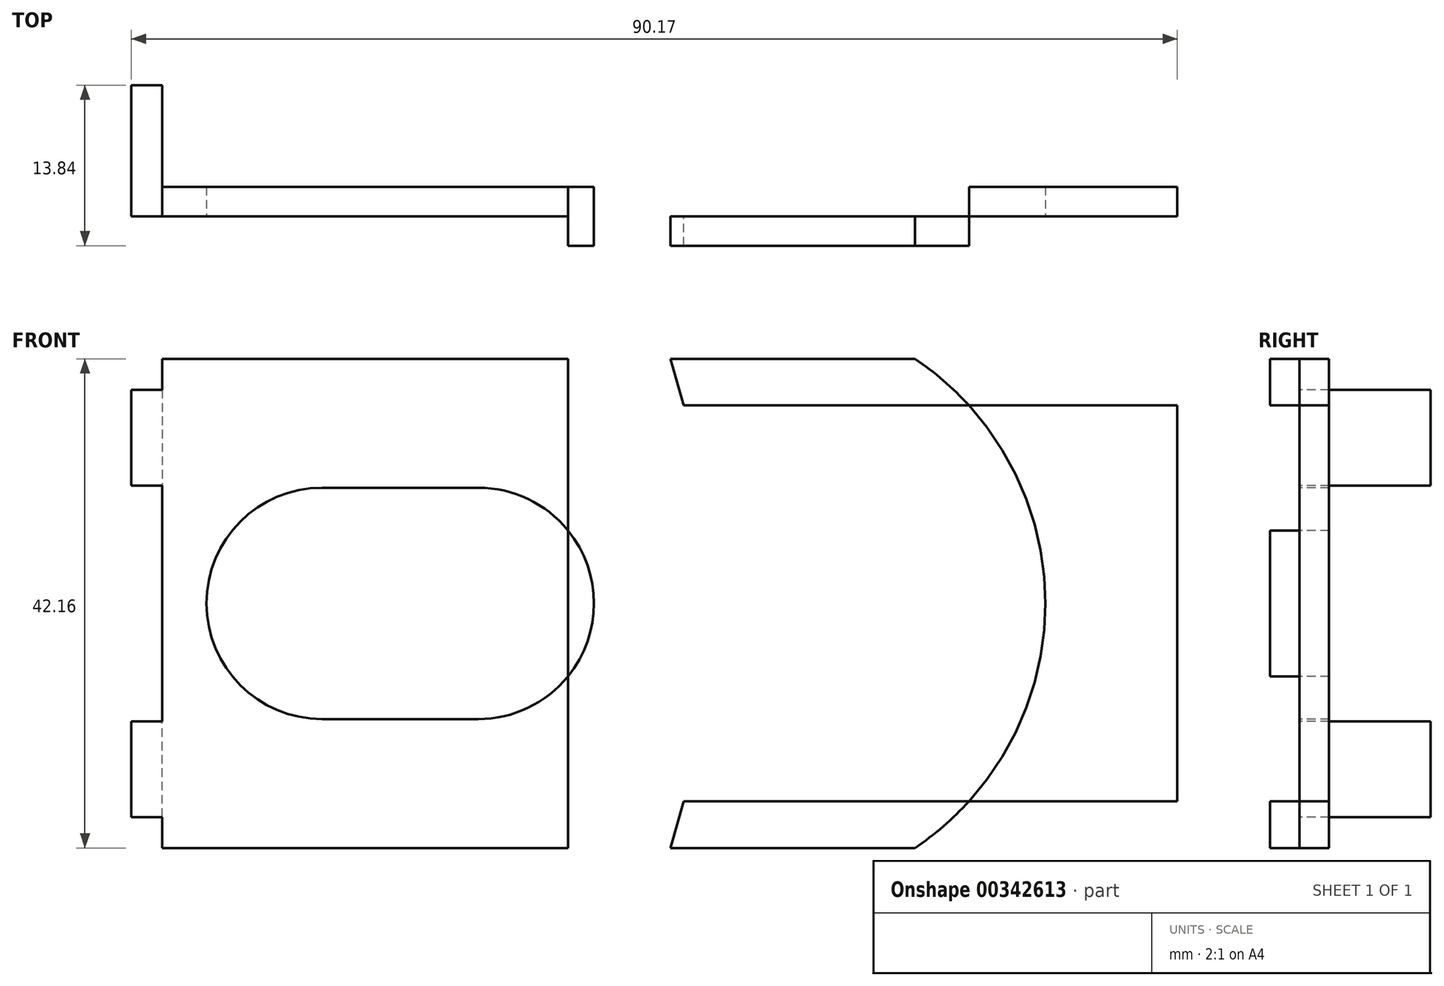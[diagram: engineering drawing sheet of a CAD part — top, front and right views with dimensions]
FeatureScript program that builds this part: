
annotation { "Feature Type Name" : "Feature", "Feature Type Description" : "" }
export const myFeature = defineFeature(function(context is Context, id is Id, definition is map)
    precondition{}
    {
        {
            var Q0;
            Q0=qCreatedBy(makeId("Front.planeOp"),FACE);
            var sketch = newSketch(context, id + "F0", { "sketchPlane" : qUnion([Q0])});
            skLineSegment(sketch, "E0.bottom", {"start": v(-47.49, 21.08) * mm, "end": v(17.4, 21.08) * mm});
            skLineSegment(sketch, "E0.left", {"start": v(-50.15, 18.41) * mm, "end": v(-50.15, 10.16) * mm});
            skLineSegment(sketch, "E0.right", {"start": v(40.02, 17.06) * mm, "end": v(40.02, 0) * mm});
            skLineSegment(sketch, "E1", {"start": v(-50.15, 10.16) * mm, "end": v(-47.49, 10.16) * mm});
            skLineSegment(sketch, "E2", {"start": v(-47.49, 10.16) * mm, "end": v(-47.49, 0) * mm});
            skLineSegment(sketch, "E3", {"start": v(-47.49, 18.41) * mm, "end": v(-47.49, 21.08) * mm});
            skLineSegment(sketch, "E4", {"start": v(-47.49, 18.41) * mm, "end": v(-50.15, 18.41) * mm});
            skPoint(sketch, "E5.orphan", {"position": v(-50.15, 21.08) * mm});
            skPoint(sketch, "E6.orphan", {"position": v(-50.15, -21.08) * mm});
            skLineSegment(sketch, "E7", {"start": v(-47.49, 0) * mm, "end": v(0, 0) * mm, "construction": true});
            skLineSegment(sketch, "E8", {"start": v(-50.15, 21.08) * mm, "end": v(-50.15, -21.08) * mm, "construction": true});
            skLineSegment(sketch, "E9", {"start": v(-50.15, 0) * mm, "end": v(-47.49, 0) * mm, "construction": true});
            skLineSegment(sketch, "E10", {"start": v(-33.7, 9.97) * mm, "end": v(-20.25, 9.97) * mm});
            skLineSegment(sketch, "E11.MirrorCS", {"start": v(-33.7, -9.97) * mm, "end": v(-20.25, -9.97) * mm});
            skArc(sketch, "E12", {"start": v(-33.7, 9.97) * mm, "mid": v(-43.68, 0) * mm, "end": v(-33.7, -9.97) * mm});
            skArc(sketch, "E13", {"start": v(-20.25, -9.97) * mm, "mid": v(-10.28, 0) * mm, "end": v(-20.25, 9.97) * mm});
            skLineSegment(sketch, "E14", {"start": v(-12.51, 21.08) * mm, "end": v(-12.51, 0) * mm});
            skArc(sketch, "E15", {"start": v(28.64, 0) * mm, "mid": v(25.65, 11.94) * mm, "end": v(17.4, 21.08) * mm});
            skLineSegment(sketch, "E16", {"start": v(40.02, 17.06) * mm, "end": v(-2.53, 17.06) * mm});
            skLineSegment(sketch, "E17", {"start": v(-2.53, 17.06) * mm, "end": v(-3.67, 21.08) * mm});
            skLineSegment(sketch, "E18.MirrorCS", {"start": v(-47.49, -21.08) * mm, "end": v(17.4, -21.08) * mm});
            skLineSegment(sketch, "E19.MirrorCS", {"start": v(40.02, -17.06) * mm, "end": v(-2.53, -17.06) * mm});
            skLineSegment(sketch, "E20.MirrorCS", {"start": v(-2.53, -17.06) * mm, "end": v(-3.67, -21.08) * mm});
            skArc(sketch, "E21.MirrorCS", {"start": v(28.64, 0) * mm, "mid": v(25.65, -11.94) * mm, "end": v(17.4, -21.08) * mm});
            skLineSegment(sketch, "E22.MirrorCS", {"start": v(40.02, -17.06) * mm, "end": v(40.02, 0) * mm});
            skLineSegment(sketch, "E23.MirrorCS", {"start": v(-47.49, -10.16) * mm, "end": v(-47.49, 0) * mm});
            skLineSegment(sketch, "E24.MirrorCS", {"start": v(-50.15, -10.16) * mm, "end": v(-47.49, -10.16) * mm});
            skLineSegment(sketch, "E25.MirrorCS", {"start": v(-50.15, -18.41) * mm, "end": v(-50.15, -10.16) * mm});
            skLineSegment(sketch, "E26.MirrorCS", {"start": v(-47.49, -18.41) * mm, "end": v(-50.15, -18.41) * mm});
            skLineSegment(sketch, "E27.MirrorCS", {"start": v(-47.49, -18.41) * mm, "end": v(-47.49, -21.08) * mm});
            skLineSegment(sketch, "E28.MirrorCS", {"start": v(-12.51, -21.08) * mm, "end": v(-12.51, 0) * mm});
            skLineSegment(sketch, "E29", {"start": v(-47.49, 18.41) * mm, "end": v(-47.49, 10.16) * mm});
            skLineSegment(sketch, "E30.MirrorCS", {"start": v(-47.49, -18.41) * mm, "end": v(-47.49, -10.16) * mm});
            skSolve(sketch);
        }
        {
            var Q0;
            {var subQ5=sQuery(id+"F0.wireOp",EDGE,"E0.right");Q0=makeQuery(id+"F0.imprint","IMPRINT",FACE,{"disambiguationData":[TD([[makeQuery(id+"F0.imprint","IMPRINT",EDGE,{"derivedFrom":subQ5}),-1.0]])]});}
            var Q1;
            Q1=makeQuery(id+"F0.imprint","IMPRINT",FACE,{"disambiguationData":[TD([[makeQuery(id+"F0.imprint","IMPRINT",EDGE,{"derivedFrom":sQuery(id+"F0.wireOp",EDGE,"E0.left")}),1.0]])]});
            var Q2;
            {var subQ1=sQuery(id+"F0.wireOp",EDGE,"E17");Q2=makeQuery(id+"F0.imprint","IMPRINT",FACE,{"disambiguationData":[TD([[makeQuery(id+"F0.imprint","IMPRINT",EDGE,{"derivedFrom":subQ1}),1.0]])]});}
            var Q3;
            {var subQ0=sQuery(id+"F0.wireOp",EDGE,"E28.MirrorCS");var subQ1=sQuery(id+"F0.wireOp",EDGE,"E13");var subQ2=makeQuery(id+"F0.imprint","INTERSECT",VERTEX,{"derivedFrom":[subQ1,subQ0]});Q3=makeQuery(id+"F0.imprint","IMPRINT",FACE,{"disambiguationData":[TD([[makeQuery(id+"F0.imprint","IMPRINT",EDGE,{"disambiguationData":[TD([[subQ2,-1.0]])],"derivedFrom":subQ1}),1.0]])]});}
            var Q4;
            Q4=makeQuery(id+"F0.imprint","IMPRINT",FACE,{"disambiguationData":[TD([[makeQuery(id+"F0.imprint","IMPRINT",EDGE,{"derivedFrom":sQuery(id+"F0.wireOp",EDGE,"E2")}),1.0]])]});
            var Q5;
            Q5=makeQuery(id+"F0.imprint","IMPRINT",FACE,{"disambiguationData":[TD([[makeQuery(id+"F0.imprint","IMPRINT",EDGE,{"derivedFrom":sQuery(id+"F0.wireOp",EDGE,"E24.MirrorCS")}),-1.0]])]});
            extrude(context, id + "F1", {"entities" : qUnion([Q0, Q1, Q2, Q3, Q4, Q5]), "oppositeDirection" : true, "depth" : 2.54 * mm});
        }
        {
            var Q0;
            {var subQ1=sQuery(id+"F0.wireOp",EDGE,"E17");Q0=makeQuery(id+"F0.imprint","IMPRINT",FACE,{"disambiguationData":[TD([[makeQuery(id+"F0.imprint","IMPRINT",EDGE,{"derivedFrom":subQ1}),1.0]])]});}
            var Q1;
            {var subQ0=sQuery(id+"F0.wireOp",EDGE,"E28.MirrorCS");var subQ1=sQuery(id+"F0.wireOp",EDGE,"E13");var subQ2=makeQuery(id+"F0.imprint","INTERSECT",VERTEX,{"derivedFrom":[subQ1,subQ0]});Q1=makeQuery(id+"F0.imprint","IMPRINT",FACE,{"disambiguationData":[TD([[makeQuery(id+"F0.imprint","IMPRINT",EDGE,{"disambiguationData":[TD([[subQ2,-1.0]])],"derivedFrom":subQ1}),1.0]])]});}
            var Q2;
            {var subQ3=sQuery(id+"F0.wireOp",EDGE,"E17");Q2=makeQuery(id+"F0.imprint","IMPRINT",FACE,{"disambiguationData":[TD([[makeQuery(id+"F0.imprint","IMPRINT",EDGE,{"derivedFrom":subQ3}),-1.0]])]});}
            var Q3;
            {var subQ3=sQuery(id+"F0.wireOp",EDGE,"E20.MirrorCS");Q3=makeQuery(id+"F0.imprint","IMPRINT",FACE,{"disambiguationData":[TD([[makeQuery(id+"F0.imprint","IMPRINT",EDGE,{"derivedFrom":subQ3}),1.0]])]});}
            extrude(context, id + "F2", {"entities" : qUnion([Q0, Q1, Q2, Q3]), "operationType" : NewBodyOperationType.ADD, "depth" : 2.54 * mm});
        }
        {
            var Q0;
            Q0=makeQuery(id+"F0.imprint","IMPRINT",FACE,{"disambiguationData":[TD([[makeQuery(id+"F0.imprint","IMPRINT",EDGE,{"derivedFrom":sQuery(id+"F0.wireOp",EDGE,"E0.left")}),1.0]])]});
            var Q1;
            Q1=makeQuery(id+"F0.imprint","IMPRINT",FACE,{"disambiguationData":[TD([[makeQuery(id+"F0.imprint","IMPRINT",EDGE,{"derivedFrom":sQuery(id+"F0.wireOp",EDGE,"E24.MirrorCS")}),-1.0]])]});
            extrude(context, id + "F3", {"entities" : qUnion([Q0, Q1]), "operationType" : NewBodyOperationType.ADD, "oppositeDirection" : true, "depth" : 11.3 * mm});
        }
    });
